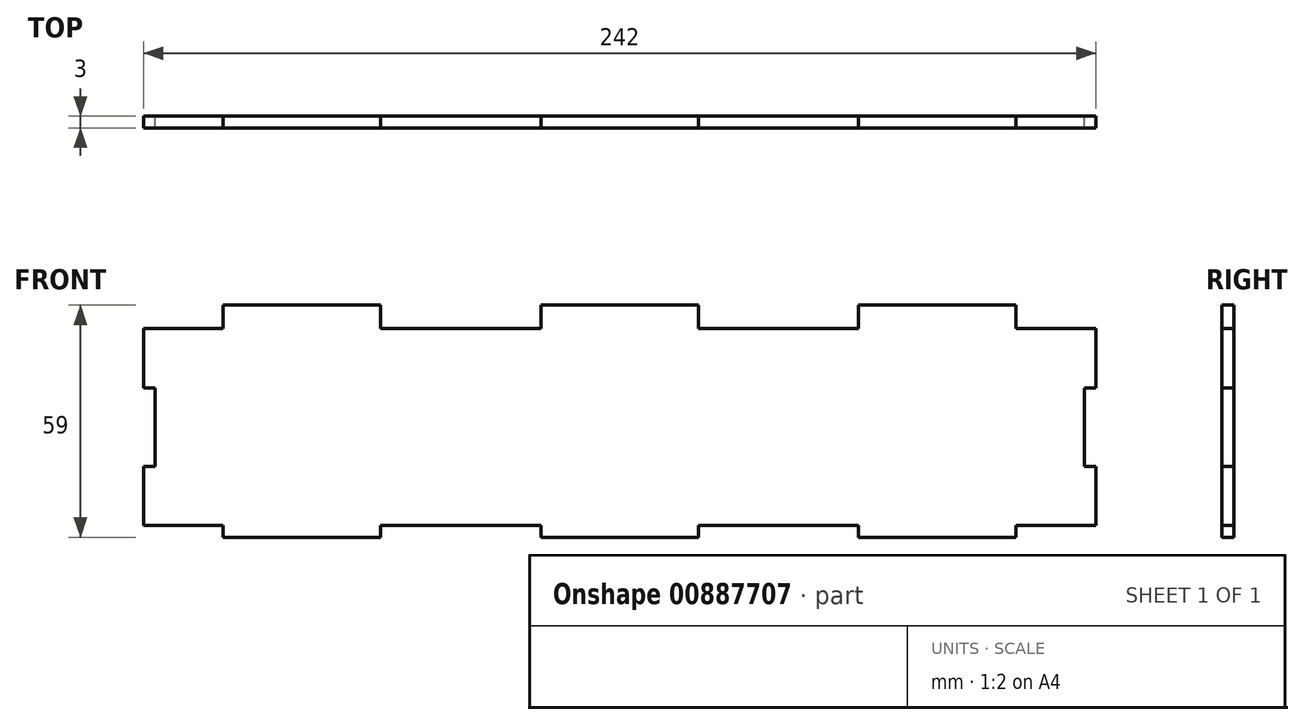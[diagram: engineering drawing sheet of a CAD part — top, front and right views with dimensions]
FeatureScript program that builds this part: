
annotation { "Feature Type Name" : "Feature", "Feature Type Description" : "" }
export const myFeature = defineFeature(function(context is Context, id is Id, definition is map)
    precondition{}
    {
        {
            var Q0;
            Q0=qCreatedBy(makeId("Front.planeOp"),FACE);
            var sketch = newSketch(context, id + "F0", { "sketchPlane" : qUnion([Q0])});
            skLineSegment(sketch, "E0.bottom", {"start": v(121, -25) * mm, "end": v(100.7, -25) * mm});
            skLineSegment(sketch, "E0.top", {"start": v(121, 25) * mm, "end": v(100.7, 25) * mm});
            skLineSegment(sketch, "E0.left", {"start": v(121, -25) * mm, "end": v(121, -10) * mm});
            skLineSegment(sketch, "E0.right", {"start": v(-121, -25) * mm, "end": v(-121, -10) * mm});
            skPoint(sketch, "E0.middle", {"position": v(0, 0) * mm});
            skLineSegment(sketch, "E1", {"start": v(-100.7, -25) * mm, "end": v(-100.7, -28) * mm});
            skLineSegment(sketch, "E2", {"start": v(-100.7, -28) * mm, "end": v(-60.7, -28) * mm});
            skLineSegment(sketch, "E3", {"start": v(-60.7, -28) * mm, "end": v(-60.7, -25) * mm});
            skLineSegment(sketch, "E4", {"start": v(-20, -25) * mm, "end": v(-20, -28) * mm});
            skLineSegment(sketch, "E5", {"start": v(-20, -28) * mm, "end": v(20, -28) * mm});
            skLineSegment(sketch, "E6", {"start": v(20, -28) * mm, "end": v(20, -25) * mm});
            skLineSegment(sketch, "E7.MirrorCS", {"start": v(100.7, -28) * mm, "end": v(60.7, -28) * mm});
            skLineSegment(sketch, "E8.MirrorCS", {"start": v(100.7, -25) * mm, "end": v(100.7, -28) * mm});
            skLineSegment(sketch, "E9.MirrorCS", {"start": v(60.7, -28) * mm, "end": v(60.7, -25) * mm});
            skLineSegment(sketch, "E10.trimOffspring", {"start": v(-100.7, -25) * mm, "end": v(-121, -25) * mm});
            skLineSegment(sketch, "E11.trimOffspring", {"start": v(-20, -25) * mm, "end": v(-60.7, -25) * mm});
            skLineSegment(sketch, "E12.trimOffspring", {"start": v(60.7, -25) * mm, "end": v(20, -25) * mm});
            skLineSegment(sketch, "E13.MirrorCS", {"start": v(-100.7, 25) * mm, "end": v(-100.7, 28) * mm});
            skLineSegment(sketch, "E14.MirrorCS", {"start": v(-60.7, 28) * mm, "end": v(-60.7, 25) * mm});
            skLineSegment(sketch, "E15.MirrorCS", {"start": v(-20, 25) * mm, "end": v(-20, 28) * mm});
            skLineSegment(sketch, "E16.MirrorCS", {"start": v(20, 28) * mm, "end": v(20, 25) * mm});
            skLineSegment(sketch, "E17.MirrorCS", {"start": v(60.7, 28) * mm, "end": v(60.7, 25) * mm});
            skLineSegment(sketch, "E18.MirrorCS", {"start": v(100.7, 25) * mm, "end": v(100.7, 28) * mm});
            skLineSegment(sketch, "E19.trimOffspring", {"start": v(-100.7, 25) * mm, "end": v(-121, 25) * mm});
            skLineSegment(sketch, "E20.trimOffspring", {"start": v(-20, 25) * mm, "end": v(-60.7, 25) * mm});
            skLineSegment(sketch, "E21.trimOffspring", {"start": v(60.7, 25) * mm, "end": v(20, 25) * mm});
            skLineSegment(sketch, "E22", {"start": v(-121, 10) * mm, "end": v(-118, 10) * mm});
            skLineSegment(sketch, "E23", {"start": v(-118, 10) * mm, "end": v(-118, -10) * mm});
            skLineSegment(sketch, "E24", {"start": v(-118, -10) * mm, "end": v(-121, -10) * mm});
            skLineSegment(sketch, "E25.trimOffspring", {"start": v(-121, 10) * mm, "end": v(-121, 25) * mm});
            skLineSegment(sketch, "E26.MirrorCS", {"start": v(118, 10) * mm, "end": v(118, -10) * mm});
            skLineSegment(sketch, "E27.MirrorCS", {"start": v(121, 10) * mm, "end": v(118, 10) * mm});
            skLineSegment(sketch, "E28.MirrorCS", {"start": v(118, -10) * mm, "end": v(121, -10) * mm});
            skLineSegment(sketch, "E29.trimOffspring", {"start": v(121, 10) * mm, "end": v(121, 25) * mm});
            skLineSegment(sketch, "E30", {"start": v(-100.7, 28) * mm, "end": v(-100.7, 31) * mm});
            skLineSegment(sketch, "E31", {"start": v(-100.7, 31) * mm, "end": v(-60.7, 31) * mm});
            skLineSegment(sketch, "E32", {"start": v(-60.7, 31) * mm, "end": v(-60.7, 28) * mm});
            skPoint(sketch, "E33.MirrorCS.start.orphan", {"position": v(-100.7, 28) * mm});
            skLineSegment(sketch, "E34.MirrorCS", {"start": v(100.7, 31) * mm, "end": v(60.7, 31) * mm});
            skLineSegment(sketch, "E35.MirrorCS", {"start": v(60.7, 31) * mm, "end": v(60.7, 28) * mm});
            skLineSegment(sketch, "E36.MirrorCS", {"start": v(100.7, 28) * mm, "end": v(100.7, 31) * mm});
            skPoint(sketch, "E37.MirrorCS.end.orphan", {"position": v(60.7, 28) * mm});
            skPoint(sketch, "E37.MirrorCS.start.orphan", {"position": v(100.7, 28) * mm});
            skLineSegment(sketch, "E38", {"start": v(-20, 28) * mm, "end": v(-20, 31) * mm});
            skLineSegment(sketch, "E39", {"start": v(-20, 31) * mm, "end": v(20, 31) * mm});
            skLineSegment(sketch, "E40", {"start": v(20, 31) * mm, "end": v(20, 28) * mm});
            skPoint(sketch, "E41.MirrorCS.start.orphan", {"position": v(-20, 28) * mm});
            skSolve(sketch);
        }
        {
            var Q0;
            Q0=qSketchRegion(id+"F0",true);
            extrude(context, id + "F1", {"entities" : qUnion([Q0]), "depth" : 3 * mm, "offsetDistance" : 25 * mm});
        }
    });
